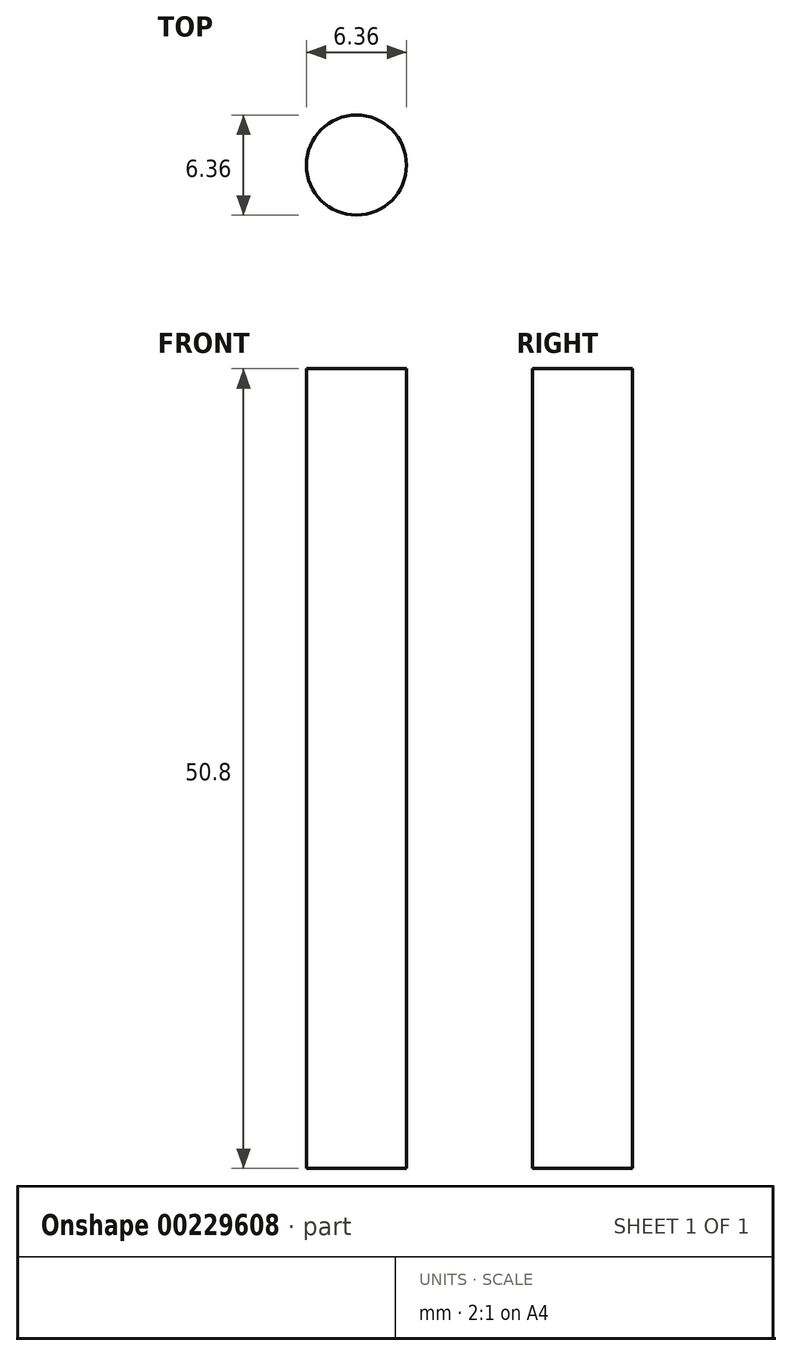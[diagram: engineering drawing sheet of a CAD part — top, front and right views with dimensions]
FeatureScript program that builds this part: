
annotation { "Feature Type Name" : "Feature", "Feature Type Description" : "" }
export const myFeature = defineFeature(function(context is Context, id is Id, definition is map)
    precondition{}
    {
        {
            var Q0;
            Q0=qCreatedBy(makeId("Top.planeOp"),FACE);
            var sketch = newSketch(context, id + "F0", { "sketchPlane" : qUnion([Q0])});
            skCircle(sketch, "E0", {"center": v(0, 0) * mm, "radius": 3.18 * mm});
            skSolve(sketch);
        }
        {
            var Q0;
            Q0=makeQuery(id+"F0.imprint","IMPRINT",FACE,{"disambiguationData":[TD([[makeQuery(id+"F0.imprint","IMPRINT",EDGE,{"derivedFrom":sQuery(id+"F0.wireOp",EDGE,"E0")}),1.0]])]});
            extrude(context, id + "F1", {"entities" : qUnion([Q0]), "depth" : 50.8 * mm});
        }
    });
